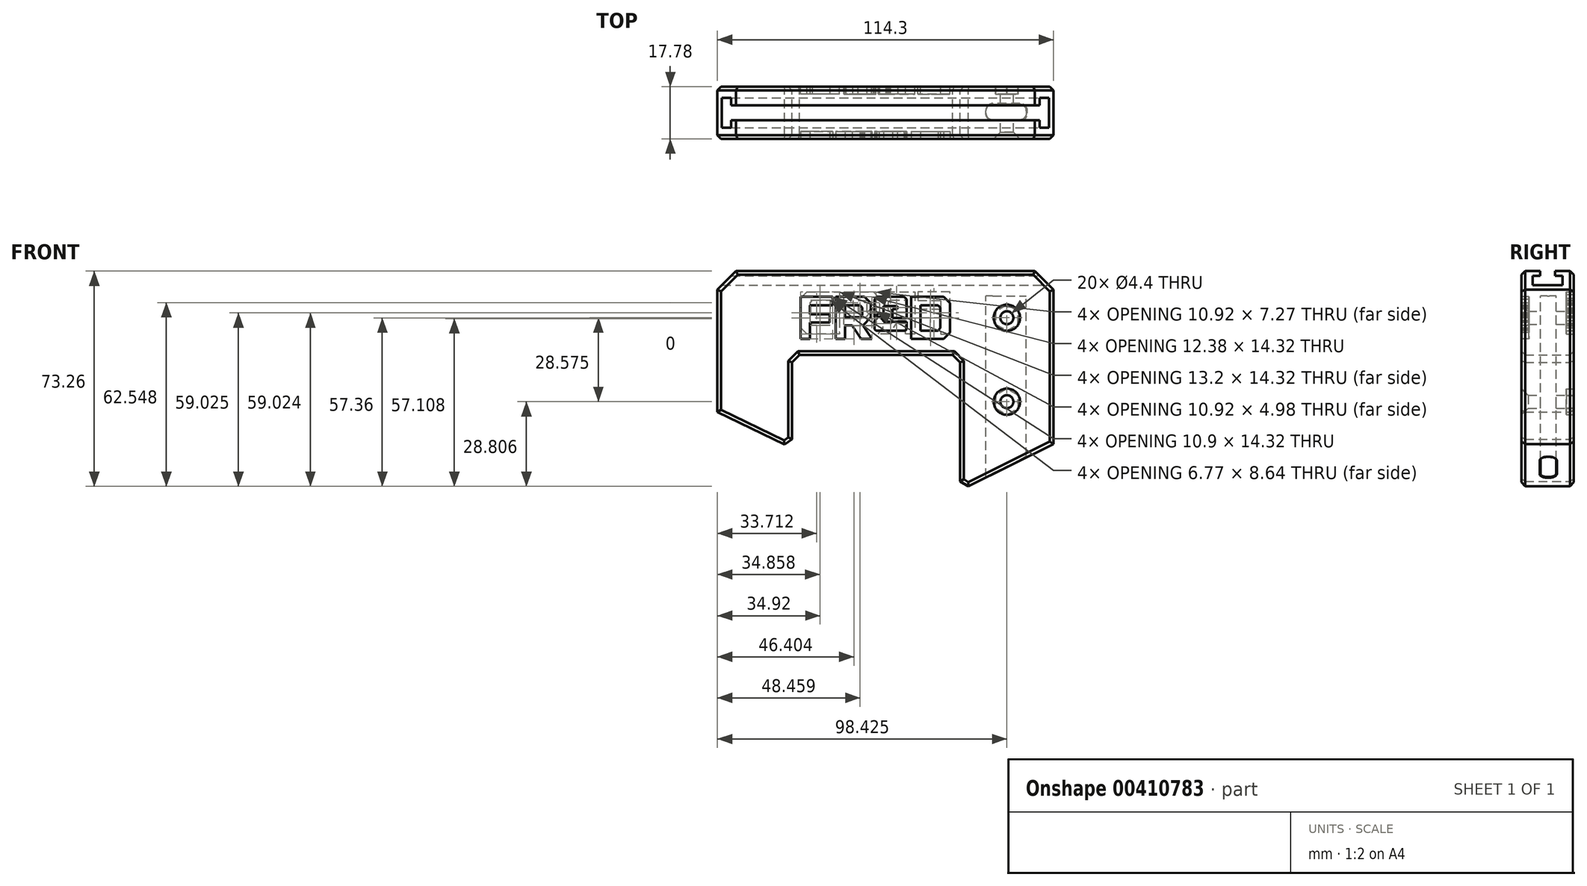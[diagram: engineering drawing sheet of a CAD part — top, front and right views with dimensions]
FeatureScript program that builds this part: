
annotation { "Feature Type Name" : "Feature", "Feature Type Description" : "" }
export const myFeature = defineFeature(function(context is Context, id is Id, definition is map)
    precondition{}
    {
        {
            var Q0;
            Q0=qCreatedBy(makeId("Front.planeOp"),FACE);
            var sketch = newSketch(context, id + "F0", { "sketchPlane" : qUnion([Q0])});
            skLineSegment(sketch, "E0", {"start": v(-47.31, 34.12) * mm, "end": v(54.29, 34.12) * mm});
            skLineSegment(sketch, "E1", {"start": v(60.64, 27.77) * mm, "end": v(60.64, -24.7) * mm});
            skLineSegment(sketch, "E2", {"start": v(60.64, -24.7) * mm, "end": v(31.6, -39.14) * mm});
            skLineSegment(sketch, "E3", {"start": v(28.89, -37.47) * mm, "end": v(28.89, 3) * mm});
            skLineSegment(sketch, "E4", {"start": v(26.35, 5.54) * mm, "end": v(-25.72, 5.54) * mm});
            skLineSegment(sketch, "E5", {"start": v(-28.26, 3) * mm, "end": v(-28.26, -23.14) * mm});
            skLineSegment(sketch, "E6", {"start": v(-30.87, -24.94) * mm, "end": v(-53.66, -13.83) * mm});
            skLineSegment(sketch, "E7", {"start": v(-53.66, -13.83) * mm, "end": v(-53.66, 27.77) * mm});
            skLineSegment(sketch, "E8", {"start": v(-30.87, -24.94) * mm, "end": v(-28.26, -23.14) * mm});
            skLineSegment(sketch, "E9", {"start": v(28.89, -37.47) * mm, "end": v(31.6, -39.14) * mm});
            skLineSegment(sketch, "E10", {"start": v(-53.66, 27.77) * mm, "end": v(-47.31, 34.12) * mm});
            skPoint(sketch, "E11.orphan", {"position": v(-53.66, 34.12) * mm});
            skLineSegment(sketch, "E12", {"start": v(54.29, 34.12) * mm, "end": v(60.64, 27.77) * mm});
            skPoint(sketch, "E13.orphan", {"position": v(60.64, 34.12) * mm});
            skLineSegment(sketch, "E14", {"start": v(-28.26, 3) * mm, "end": v(-25.72, 5.54) * mm});
            skPoint(sketch, "E15.orphan", {"position": v(-28.26, 5.54) * mm});
            skLineSegment(sketch, "E16", {"start": v(26.35, 5.54) * mm, "end": v(28.89, 3) * mm});
            skPoint(sketch, "E17.orphan", {"position": v(28.89, 5.54) * mm});
            skSolve(sketch);
        }
        {
            var Q0;
            Q0=makeQuery(id+"F0.imprint","IMPRINT",FACE,{"disambiguationData":[TD([[makeQuery(id+"F0.imprint","IMPRINT",EDGE,{"derivedFrom":sQuery(id+"F0.wireOp",EDGE,"E0")}),-1.0]])]});
            var Q1;
            Q1=makeQuery(id+"F0.imprint","IMPRINT",FACE,{"disambiguationData":[TD([[makeQuery(id+"F0.imprint","IMPRINT",EDGE,{"derivedFrom":sQuery(id+"F0.wireOp",EDGE,"ZEpFWphL-ozMd-Qc4S-y12z-fugVZn2PExex")}),1.0]])]});
            var Q2;
            Q2=makeQuery(id+"F0.imprint","IMPRINT",FACE,{"disambiguationData":[TD([[makeQuery(id+"F0.imprint","IMPRINT",EDGE,{"derivedFrom":sQuery(id+"F0.wireOp",EDGE,"a8f3txKb-fRa5-LG7a-W4z5-OOKFphKNCb56")}),1.0]])]});
            extrude(context, id + "F1", {"entities" : qUnion([Q0, Q1, Q2]), "depth" : 17.78 * mm, "offsetDistance" : 25.4 * mm, "symmetric" : true});
        }
        {
            var Q0;
            Q0=qCreatedBy(makeId("Top.planeOp"),FACE);
            var sketch = newSketch(context, id + "F2", { "sketchPlane" : qUnion([Q0])});
            skLineSegment(sketch, "E18.bottom", {"start": v(39.94, -2.42) * mm, "end": v(49.08, -2.42) * mm});
            skLineSegment(sketch, "E18.top", {"start": v(39.94, 2.92) * mm, "end": v(49.08, 2.92) * mm});
            skLineSegment(sketch, "E18.left", {"start": v(37.65, -0.13) * mm, "end": v(37.65, 0.63) * mm});
            skLineSegment(sketch, "E18.right", {"start": v(51.37, -0.13) * mm, "end": v(51.37, 0.63) * mm});
            skPoint(sketch, "E19.visualSharp", {"position": v(37.65, -2.42) * mm});
            skArc(sketch, "E19.filletArc", {"start": v(37.65, -0.13) * mm, "mid": v(38.32, -1.75) * mm, "end": v(39.94, -2.42) * mm});
            skPoint(sketch, "E20.visualSharp", {"position": v(37.65, 2.92) * mm});
            skArc(sketch, "E20.filletArc", {"start": v(39.94, 2.92) * mm, "mid": v(38.32, 2.25) * mm, "end": v(37.65, 0.63) * mm});
            skPoint(sketch, "E21.visualSharp", {"position": v(51.37, 2.92) * mm});
            skArc(sketch, "E21.filletArc", {"start": v(51.37, 0.63) * mm, "mid": v(50.7, 2.25) * mm, "end": v(49.08, 2.92) * mm});
            skPoint(sketch, "E22.visualSharp", {"position": v(51.37, -2.42) * mm});
            skArc(sketch, "E22.filletArc", {"start": v(49.08, -2.42) * mm, "mid": v(50.7, -1.75) * mm, "end": v(51.37, -0.13) * mm});
            skSolve(sketch);
        }
        {
            var Q0;
            Q0=makeQuery(id+"F2.imprint","IMPRINT",FACE,{"disambiguationData":[TD([[makeQuery(id+"F2.imprint","IMPRINT",EDGE,{"derivedFrom":sQuery(id+"F2.wireOp",EDGE,"E18.bottom")}),1.0]])]});
            extrude(context, id + "F3", {"entities" : qUnion([Q0]), "operationType" : NewBodyOperationType.REMOVE, "oppositeDirection" : true, "depth" : 59.33 * mm, "offsetDistance" : 25.4 * mm, "hasSecondDirection" : true, "secondDirectionOppositeDirection" : false, "secondDirectionDepth" : 25.65 * mm});
        }
        {
            var Q0;
            Q0=makeQuery(id+"F1.opExtrude","CAP_EDGE",EDGE,{"disambiguationData":[OSD([sQuery(id+"F0.wireOp",EDGE,"E0")])],"isStart":false});
            var Q1;
            Q1=makeQuery(id+"F1.opExtrude","CAP_EDGE",EDGE,{"disambiguationData":[OSD([sQuery(id+"F0.wireOp",EDGE,"E12")])],"isStart":false});
            var Q2;
            Q2=makeQuery(id+"F1.opExtrude","CAP_EDGE",EDGE,{"disambiguationData":[OSD([sQuery(id+"F0.wireOp",EDGE,"E1")])],"isStart":false});
            var Q3;
            Q3=makeQuery(id+"F1.opExtrude","CAP_EDGE",EDGE,{"disambiguationData":[OSD([sQuery(id+"F0.wireOp",EDGE,"E4")])],"isStart":false});
            var Q4;
            Q4=makeQuery(id+"F1.opExtrude","CAP_EDGE",EDGE,{"disambiguationData":[OSD([sQuery(id+"F0.wireOp",EDGE,"E16")])],"isStart":false});
            var Q5;
            Q5=makeQuery(id+"F1.opExtrude","CAP_EDGE",EDGE,{"disambiguationData":[OSD([sQuery(id+"F0.wireOp",EDGE,"E3")])],"isStart":false});
            var Q6;
            Q6=makeQuery(id+"F1.opExtrude","CAP_EDGE",EDGE,{"disambiguationData":[OSD([sQuery(id+"F0.wireOp",EDGE,"E9")])],"isStart":false});
            var Q7;
            Q7=makeQuery(id+"F1.opExtrude","CAP_EDGE",EDGE,{"disambiguationData":[OSD([sQuery(id+"F0.wireOp",EDGE,"E2")])],"isStart":false});
            var Q8;
            Q8=makeQuery(id+"F1.opExtrude","CAP_EDGE",EDGE,{"disambiguationData":[OSD([sQuery(id+"F0.wireOp",EDGE,"E1")])],"isStart":true});
            var Q9;
            Q9=makeQuery(id+"F1.opExtrude","CAP_EDGE",EDGE,{"disambiguationData":[OSD([sQuery(id+"F0.wireOp",EDGE,"E2")])],"isStart":true});
            var Q10;
            Q10=makeQuery(id+"F1.opExtrude","CAP_EDGE",EDGE,{"disambiguationData":[OSD([sQuery(id+"F0.wireOp",EDGE,"E12")])],"isStart":true});
            var Q11;
            Q11=makeQuery(id+"F1.opExtrude","CAP_EDGE",EDGE,{"disambiguationData":[OSD([sQuery(id+"F0.wireOp",EDGE,"E0")])],"isStart":true});
            var Q12;
            Q12=makeQuery(id+"F1.opExtrude","CAP_EDGE",EDGE,{"disambiguationData":[OSD([sQuery(id+"F0.wireOp",EDGE,"E3")])],"isStart":true});
            var Q13;
            Q13=makeQuery(id+"F1.opExtrude","CAP_EDGE",EDGE,{"disambiguationData":[OSD([sQuery(id+"F0.wireOp",EDGE,"E9")])],"isStart":true});
            var Q14;
            Q14=makeQuery(id+"F1.opExtrude","CAP_EDGE",EDGE,{"disambiguationData":[OSD([sQuery(id+"F0.wireOp",EDGE,"E16")])],"isStart":true});
            var Q15;
            Q15=makeQuery(id+"F1.opExtrude","CAP_EDGE",EDGE,{"disambiguationData":[OSD([sQuery(id+"F0.wireOp",EDGE,"E4")])],"isStart":true});
            var Q16;
            Q16=makeQuery(id+"F1.opExtrude","CAP_EDGE",EDGE,{"disambiguationData":[OSD([sQuery(id+"F0.wireOp",EDGE,"E14")])],"isStart":true});
            var Q17;
            Q17=makeQuery(id+"F1.opExtrude","CAP_EDGE",EDGE,{"disambiguationData":[OSD([sQuery(id+"F0.wireOp",EDGE,"E5")])],"isStart":true});
            var Q18;
            Q18=makeQuery(id+"F1.opExtrude","CAP_EDGE",EDGE,{"disambiguationData":[OSD([sQuery(id+"F0.wireOp",EDGE,"E8")])],"isStart":true});
            var Q19;
            Q19=makeQuery(id+"F1.opExtrude","CAP_EDGE",EDGE,{"disambiguationData":[OSD([sQuery(id+"F0.wireOp",EDGE,"E6")])],"isStart":true});
            var Q20;
            Q20=makeQuery(id+"F1.opExtrude","CAP_EDGE",EDGE,{"disambiguationData":[OSD([sQuery(id+"F0.wireOp",EDGE,"E7")])],"isStart":true});
            var Q21;
            Q21=makeQuery(id+"F1.opExtrude","CAP_EDGE",EDGE,{"disambiguationData":[OSD([sQuery(id+"F0.wireOp",EDGE,"E10")])],"isStart":true});
            var Q22;
            Q22=makeQuery(id+"F1.opExtrude","CAP_EDGE",EDGE,{"disambiguationData":[OSD([sQuery(id+"F0.wireOp",EDGE,"E10")])],"isStart":false});
            var Q23;
            Q23=makeQuery(id+"F1.opExtrude","CAP_EDGE",EDGE,{"disambiguationData":[OSD([sQuery(id+"F0.wireOp",EDGE,"E7")])],"isStart":false});
            var Q24;
            Q24=makeQuery(id+"F1.opExtrude","CAP_EDGE",EDGE,{"disambiguationData":[OSD([sQuery(id+"F0.wireOp",EDGE,"E6")])],"isStart":false});
            var Q25;
            Q25=makeQuery(id+"F1.opExtrude","CAP_EDGE",EDGE,{"disambiguationData":[OSD([sQuery(id+"F0.wireOp",EDGE,"E8")])],"isStart":false});
            var Q26;
            Q26=makeQuery(id+"F1.opExtrude","CAP_EDGE",EDGE,{"disambiguationData":[OSD([sQuery(id+"F0.wireOp",EDGE,"E5")])],"isStart":false});
            var Q27;
            Q27=makeQuery(id+"F1.opExtrude","CAP_EDGE",EDGE,{"disambiguationData":[OSD([sQuery(id+"F0.wireOp",EDGE,"E14")])],"isStart":false});
            chamfer(context, id + "F4", {"entities" : qUnion([Q0, Q1, Q2, Q3, Q4, Q5, Q6, Q7, Q8, Q9, Q10, Q11, Q12, Q13, Q14, Q15, Q16, Q17, Q18, Q19, Q20, Q21, Q22, Q23, Q24, Q25, Q26, Q27]), "width" : 1.27 * mm, "tangentPropagation" : true});
        }
        {
            var Q0;
            Q0=makeQuery(id+"F3.boolean.opBoolean","INTERSECT",EDGE,{"derivedFrom":[makeQuery(id+"F1.opExtrude","SWEPT_FACE",FACE,{"disambiguationData":[OSD([sQuery(id+"F0.wireOp",EDGE,"E2")])]}),makeQuery(id+"F3.opExtrude","SWEPT_FACE",FACE,{"disambiguationData":[OSD([sQuery(id+"F2.wireOp",EDGE,"E18.bottom")])]})]});
            chamfer(context, id + "F5", {"entities" : qUnion([Q0]), "width" : 0.25 * mm, "tangentPropagation" : true});
        }
        {
            var Q0;
            Q0=makeQuery(id+"F1.opExtrude","CAP_FACE",FACE,{"disambiguationData":[OSD([sQuery(id+"F0.wireOp",EDGE,"E0"),sQuery(id+"F0.wireOp",EDGE,"E1"),sQuery(id+"F0.wireOp",EDGE,"E2"),sQuery(id+"F0.wireOp",EDGE,"E3"),sQuery(id+"F0.wireOp",EDGE,"E4"),sQuery(id+"F0.wireOp",EDGE,"E5"),sQuery(id+"F0.wireOp",EDGE,"E6"),sQuery(id+"F0.wireOp",EDGE,"E7"),sQuery(id+"F0.wireOp",EDGE,"E8"),sQuery(id+"F0.wireOp",EDGE,"E9"),sQuery(id+"F0.wireOp",EDGE,"E10"),sQuery(id+"F0.wireOp",EDGE,"E12"),sQuery(id+"F0.wireOp",EDGE,"E14"),sQuery(id+"F0.wireOp",EDGE,"E16")])],"isStart":false});
            var sketch = newSketch(context, id + "F6", { "sketchPlane" : qUnion([Q0])});
            skCircle(sketch, "E23", {"center": v(44.76, 18.24) * mm, "radius": 1.9 * mm});
            skCircle(sketch, "E24", {"center": v(44.76, -10.33) * mm, "radius": 1.9 * mm});
            skSolve(sketch);
        }
        {
            var Q0;
            Q0=sQuery(id+"F6.wireOp",VERTEX,"E23.center");
            var Q1;
            Q1=sQuery(id+"F6.wireOp",VERTEX,"E24.center");
            var Q2;
            Q2=makeQuery(id+"F1.opExtrude","SWEPT_BODY",BODY,{"disambiguationData":[OSD([sQuery(id+"F0.wireOp",EDGE,"E0"),sQuery(id+"F0.wireOp",EDGE,"E1"),sQuery(id+"F0.wireOp",EDGE,"E2"),sQuery(id+"F0.wireOp",EDGE,"E3"),sQuery(id+"F0.wireOp",EDGE,"E4"),sQuery(id+"F0.wireOp",EDGE,"E5"),sQuery(id+"F0.wireOp",EDGE,"E6"),sQuery(id+"F0.wireOp",EDGE,"E7"),sQuery(id+"F0.wireOp",EDGE,"E8"),sQuery(id+"F0.wireOp",EDGE,"E9"),sQuery(id+"F0.wireOp",EDGE,"E10"),sQuery(id+"F0.wireOp",EDGE,"E12"),sQuery(id+"F0.wireOp",EDGE,"E14"),sQuery(id+"F0.wireOp",EDGE,"E16")])]});
            hole(context, id + "F7", {"style" : HoleStyle.C_SINK, "endStyle" : HoleEndStyle.THROUGH, "standardTappedOrClearance" : lookupTablePath({ "standard" : "ISO", "fit" : "Normal", "size" : "M4", "type" : "Clearance" }), "standardBlindInLast" : lookupTablePath({ "fit" : "Standard", "standard" : "ISO", "size" : "M4", "type" : "Clearance" }), "holeDiameter" : 4.4 * mm, "cSinkDiameter" : 8.96 * mm, "cSinkAngle" : 90 * degree, "isTappedThrough" : true, "tappedDepth" : 12.7 * mm, "tapClearance" : 3, "locations" : qUnion([Q0, Q1]), "scope" : qUnion([Q2]), "startStyle" : HoleStartStyle.PART});
        }
        {
            var Q0;
            Q0=makeQuery(id+"F1.opExtrude","CAP_FACE",FACE,{"disambiguationData":[OSD([sQuery(id+"F0.wireOp",EDGE,"E0"),sQuery(id+"F0.wireOp",EDGE,"E1"),sQuery(id+"F0.wireOp",EDGE,"E2"),sQuery(id+"F0.wireOp",EDGE,"E3"),sQuery(id+"F0.wireOp",EDGE,"E4"),sQuery(id+"F0.wireOp",EDGE,"E5"),sQuery(id+"F0.wireOp",EDGE,"E6"),sQuery(id+"F0.wireOp",EDGE,"E7"),sQuery(id+"F0.wireOp",EDGE,"E8"),sQuery(id+"F0.wireOp",EDGE,"E9"),sQuery(id+"F0.wireOp",EDGE,"E10"),sQuery(id+"F0.wireOp",EDGE,"E12"),sQuery(id+"F0.wireOp",EDGE,"E14"),sQuery(id+"F0.wireOp",EDGE,"E16")])],"isStart":true});
            var sketch = newSketch(context, id + "F8", { "sketchPlane" : qUnion([Q0])});
            skCircle(sketch, "E25.cCircle", {"center": v(-44.76, 18.24) * mm, "radius": 3.8 * mm, "construction": true});
            skLineSegment(sketch, "E25.0", {"start": v(-48.57, 16.04) * mm, "end": v(-48.57, 20.44) * mm});
            skLineSegment(sketch, "E25.1", {"start": v(-48.57, 20.44) * mm, "end": v(-44.76, 22.64) * mm});
            skLineSegment(sketch, "E25.2", {"start": v(-44.76, 22.64) * mm, "end": v(-40.95, 20.44) * mm});
            skLineSegment(sketch, "E25.3", {"start": v(-40.95, 20.44) * mm, "end": v(-40.95, 16.04) * mm});
            skLineSegment(sketch, "E25.4", {"start": v(-40.95, 16.04) * mm, "end": v(-44.76, 13.84) * mm});
            skLineSegment(sketch, "E25.5", {"start": v(-44.76, 13.84) * mm, "end": v(-48.57, 16.04) * mm});
            skPoint(sketch, "E25.0.midPoint", {"position": v(-48.57, 18.24) * mm});
            skCircle(sketch, "E26.cCircle", {"center": v(-44.76, -10.33) * mm, "radius": 3.81 * mm, "construction": true});
            skLineSegment(sketch, "E26.0", {"start": v(-48.54, -8.07) * mm, "end": v(-44.69, -5.94) * mm});
            skLineSegment(sketch, "E26.1", {"start": v(-44.69, -5.94) * mm, "end": v(-40.92, -8.2) * mm});
            skLineSegment(sketch, "E26.2", {"start": v(-40.92, -8.2) * mm, "end": v(-41, -12.6) * mm});
            skLineSegment(sketch, "E26.3", {"start": v(-41, -12.6) * mm, "end": v(-44.84, -14.73) * mm});
            skLineSegment(sketch, "E26.4", {"start": v(-44.84, -14.73) * mm, "end": v(-48.61, -12.47) * mm});
            skLineSegment(sketch, "E26.5", {"start": v(-48.61, -12.47) * mm, "end": v(-48.54, -8.07) * mm});
            skPoint(sketch, "E26.0.midPoint", {"position": v(-46.61, -7) * mm});
            skSolve(sketch);
        }
        {
            var Q0;
            Q0=makeQuery(id+"F8.imprint","IMPRINT",FACE,{"disambiguationData":[TD([[makeQuery(id+"F8.imprint","IMPRINT",EDGE,{"derivedFrom":sQuery(id+"F8.wireOp",EDGE,"E25.0")}),-1.0]])]});
            var Q1;
            Q1=makeQuery(id+"F8.imprint","IMPRINT",FACE,{"disambiguationData":[TD([[makeQuery(id+"F8.imprint","IMPRINT",EDGE,{"derivedFrom":sQuery(id+"F8.wireOp",EDGE,"E26.0")}),-1.0]])]});
            extrude(context, id + "F9", {"entities" : qUnion([Q0, Q1]), "operationType" : NewBodyOperationType.REMOVE, "oppositeDirection" : true, "depth" : 2.54 * mm, "offsetDistance" : 25.4 * mm});
        }
        {
            var Q0;
            Q0=makeQuery(id+"F1.opExtrude","CAP_FACE",FACE,{"disambiguationData":[OSD([sQuery(id+"F0.wireOp",EDGE,"E0"),sQuery(id+"F0.wireOp",EDGE,"E1"),sQuery(id+"F0.wireOp",EDGE,"E2"),sQuery(id+"F0.wireOp",EDGE,"E3"),sQuery(id+"F0.wireOp",EDGE,"E4"),sQuery(id+"F0.wireOp",EDGE,"E5"),sQuery(id+"F0.wireOp",EDGE,"E6"),sQuery(id+"F0.wireOp",EDGE,"E7"),sQuery(id+"F0.wireOp",EDGE,"E8"),sQuery(id+"F0.wireOp",EDGE,"E9"),sQuery(id+"F0.wireOp",EDGE,"E10"),sQuery(id+"F0.wireOp",EDGE,"E12"),sQuery(id+"F0.wireOp",EDGE,"E14"),sQuery(id+"F0.wireOp",EDGE,"E16")])],"isStart":false});
            var sketch = newSketch(context, id + "F10", { "sketchPlane" : qUnion([Q0])});
            skLineSegment(sketch, "E27", {"start": v(-25.4, 25.38) * mm, "end": v(-14.5, 25.38) * mm});
            skLineSegment(sketch, "E28", {"start": v(-14.5, 25.38) * mm, "end": v(-14.5, 22.52) * mm});
            skLineSegment(sketch, "E29", {"start": v(-14.5, 22.52) * mm, "end": v(-22.25, 22.52) * mm});
            skLineSegment(sketch, "E30", {"start": v(-22.25, 22.52) * mm, "end": v(-22.25, 19.47) * mm});
            skLineSegment(sketch, "E31", {"start": v(-22.25, 19.47) * mm, "end": v(-15.42, 19.47) * mm});
            skLineSegment(sketch, "E32", {"start": v(-15.42, 19.47) * mm, "end": v(-15.42, 16.6) * mm});
            skLineSegment(sketch, "E33", {"start": v(-15.42, 16.6) * mm, "end": v(-22.25, 16.6) * mm});
            skLineSegment(sketch, "E34", {"start": v(-22.25, 16.6) * mm, "end": v(-22.25, 11.06) * mm});
            skLineSegment(sketch, "E35", {"start": v(-22.25, 11.06) * mm, "end": v(-25.4, 11.06) * mm});
            skLineSegment(sketch, "E36", {"start": v(-25.4, 11.06) * mm, "end": v(-25.4, 25.38) * mm});
            skLineSegment(sketch, "E37", {"start": v(2.84, 16.91) * mm, "end": v(2.84, 17.23) * mm});
            skLineSegment(sketch, "E38", {"start": v(2.84, 17.23) * mm, "end": v(1.3, 18.8) * mm});
            skLineSegment(sketch, "E39", {"start": v(1.3, 18.8) * mm, "end": v(-0.26, 17.23) * mm});
            skLineSegment(sketch, "E40", {"start": v(-0.26, 17.23) * mm, "end": v(-0.26, 16.91) * mm});
            skLineSegment(sketch, "E41", {"start": v(-0.26, 16.91) * mm, "end": v(-0.26, 14.47) * mm});
            skLineSegment(sketch, "E42", {"start": v(-0.26, 14.47) * mm, "end": v(-0.26, 14.3) * mm});
            skLineSegment(sketch, "E43", {"start": v(-0.26, 14.3) * mm, "end": v(0.23, 13.81) * mm});
            skLineSegment(sketch, "E44", {"start": v(0.23, 13.81) * mm, "end": v(10.17, 13.81) * mm});
            skLineSegment(sketch, "E45", {"start": v(10.17, 13.81) * mm, "end": v(10.66, 14.3) * mm});
            skLineSegment(sketch, "E46", {"start": v(10.66, 14.3) * mm, "end": v(10.66, 16.91) * mm});
            skLineSegment(sketch, "E47", {"start": v(10.66, 16.91) * mm, "end": v(2.84, 16.91) * mm});
            skLineSegment(sketch, "E48", {"start": v(-0.26, 24.56) * mm, "end": v(-0.26, 22.28) * mm});
            skLineSegment(sketch, "E49", {"start": v(-0.26, 22.28) * mm, "end": v(-0.26, 18.38) * mm});
            skLineSegment(sketch, "E50", {"start": v(-0.26, 18.38) * mm, "end": v(1.3, 19.94) * mm});
            skLineSegment(sketch, "E51", {"start": v(1.3, 19.94) * mm, "end": v(2.84, 18.38) * mm});
            skLineSegment(sketch, "E52", {"start": v(2.84, 18.38) * mm, "end": v(2.84, 22.28) * mm});
            skLineSegment(sketch, "E53", {"start": v(2.84, 22.28) * mm, "end": v(7.56, 22.28) * mm});
            skLineSegment(sketch, "E54", {"start": v(7.56, 22.28) * mm, "end": v(7.56, 21.2) * mm});
            skLineSegment(sketch, "E55", {"start": v(7.56, 21.2) * mm, "end": v(5.87, 21.2) * mm});
            skLineSegment(sketch, "E56", {"start": v(5.87, 21.2) * mm, "end": v(5.87, 18.1) * mm});
            skLineSegment(sketch, "E57", {"start": v(5.87, 18.1) * mm, "end": v(10.66, 18.1) * mm});
            skLineSegment(sketch, "E58", {"start": v(10.66, 18.1) * mm, "end": v(10.66, 19.48) * mm});
            skLineSegment(sketch, "E59", {"start": v(10.66, 19.48) * mm, "end": v(10.66, 21.2) * mm});
            skLineSegment(sketch, "E60", {"start": v(10.66, 21.2) * mm, "end": v(10.66, 22.28) * mm});
            skLineSegment(sketch, "E61", {"start": v(10.66, 22.28) * mm, "end": v(10.66, 24.56) * mm});
            skLineSegment(sketch, "E62", {"start": v(10.66, 24.56) * mm, "end": v(9.84, 25.38) * mm});
            skLineSegment(sketch, "E63", {"start": v(9.84, 25.38) * mm, "end": v(2.84, 25.38) * mm});
            skLineSegment(sketch, "E64", {"start": v(2.84, 25.38) * mm, "end": v(0.56, 25.38) * mm});
            skLineSegment(sketch, "E65", {"start": v(0.56, 25.38) * mm, "end": v(-0.26, 24.56) * mm});
            skLineSegment(sketch, "E66", {"start": v(-4.22, 15.66) * mm, "end": v(-1.51, 18.46) * mm});
            skLineSegment(sketch, "E67", {"start": v(-1.51, 18.46) * mm, "end": v(-1.51, 23.23) * mm});
            skLineSegment(sketch, "E68", {"start": v(-1.51, 23.23) * mm, "end": v(-3.66, 25.38) * mm});
            skLineSegment(sketch, "E69", {"start": v(-3.66, 25.38) * mm, "end": v(-13.45, 25.38) * mm});
            skLineSegment(sketch, "E70", {"start": v(-13.45, 25.38) * mm, "end": v(-13.45, 11.06) * mm});
            skLineSegment(sketch, "E71", {"start": v(-13.45, 11.06) * mm, "end": v(-10.3, 11.06) * mm});
            skLineSegment(sketch, "E72", {"start": v(-10.3, 11.06) * mm, "end": v(-10.3, 15.64) * mm});
            skLineSegment(sketch, "E73", {"start": v(-10.3, 15.64) * mm, "end": v(-7.82, 15.64) * mm});
            skLineSegment(sketch, "E74", {"start": v(-7.82, 15.64) * mm, "end": v(-4.75, 11.06) * mm});
            skLineSegment(sketch, "E75", {"start": v(-4.75, 11.06) * mm, "end": v(-1.07, 11.06) * mm});
            skLineSegment(sketch, "E76", {"start": v(-1.07, 11.06) * mm, "end": v(-4.22, 15.66) * mm});
            skLineSegment(sketch, "E77", {"start": v(17.94, 11.06) * mm, "end": v(23.17, 11.06) * mm});
            skLineSegment(sketch, "E78", {"start": v(23.17, 11.06) * mm, "end": v(23.25, 11.06) * mm});
            skLineSegment(sketch, "E79", {"start": v(23.25, 11.06) * mm, "end": v(25.4, 13.2) * mm});
            skLineSegment(sketch, "E80", {"start": v(25.4, 13.2) * mm, "end": v(25.4, 17.98) * mm});
            skLineSegment(sketch, "E81", {"start": v(25.4, 17.98) * mm, "end": v(25.4, 18.46) * mm});
            skLineSegment(sketch, "E82", {"start": v(25.4, 18.46) * mm, "end": v(25.4, 23.23) * mm});
            skLineSegment(sketch, "E83", {"start": v(25.4, 23.23) * mm, "end": v(23.25, 25.38) * mm});
            skLineSegment(sketch, "E84", {"start": v(23.25, 25.38) * mm, "end": v(23.17, 25.38) * mm});
            skLineSegment(sketch, "E85", {"start": v(23.17, 25.38) * mm, "end": v(17.94, 25.38) * mm});
            skLineSegment(sketch, "E86", {"start": v(17.94, 25.38) * mm, "end": v(17.79, 25.38) * mm});
            skLineSegment(sketch, "E87", {"start": v(17.79, 25.38) * mm, "end": v(12.2, 25.38) * mm});
            skLineSegment(sketch, "E88", {"start": v(12.2, 25.38) * mm, "end": v(12.2, 11.06) * mm});
            skLineSegment(sketch, "E89", {"start": v(12.2, 11.06) * mm, "end": v(17.79, 11.06) * mm});
            skLineSegment(sketch, "E90", {"start": v(17.79, 11.06) * mm, "end": v(17.94, 11.06) * mm});
            skLineSegment(sketch, "E91", {"start": v(-5.22, 18.4) * mm, "end": v(-4.4, 19.2) * mm});
            skLineSegment(sketch, "E92", {"start": v(-4.4, 19.2) * mm, "end": v(-4.4, 21.72) * mm});
            skLineSegment(sketch, "E93", {"start": v(-4.4, 21.72) * mm, "end": v(-5.22, 22.54) * mm});
            skLineSegment(sketch, "E94", {"start": v(-5.22, 22.54) * mm, "end": v(-10.3, 22.54) * mm});
            skLineSegment(sketch, "E95", {"start": v(-10.3, 22.54) * mm, "end": v(-10.3, 18.4) * mm});
            skLineSegment(sketch, "E96", {"start": v(-10.3, 18.4) * mm, "end": v(-5.22, 18.4) * mm});
            skLineSegment(sketch, "E97", {"start": v(21.3, 13.9) * mm, "end": v(22.13, 14.72) * mm});
            skLineSegment(sketch, "E98", {"start": v(22.13, 14.72) * mm, "end": v(22.13, 21.72) * mm});
            skLineSegment(sketch, "E99", {"start": v(22.13, 21.72) * mm, "end": v(21.3, 22.54) * mm});
            skLineSegment(sketch, "E100", {"start": v(21.3, 22.54) * mm, "end": v(15.35, 22.54) * mm});
            skLineSegment(sketch, "E101", {"start": v(15.35, 22.54) * mm, "end": v(15.35, 13.9) * mm});
            skLineSegment(sketch, "E102", {"start": v(15.35, 13.9) * mm, "end": v(21.3, 13.9) * mm});
            skSolve(sketch);
        }
        {
            var Q0;
            Q0=makeQuery(id+"F10.imprint","IMPRINT",FACE,{"disambiguationData":[TD([[makeQuery(id+"F10.imprint","IMPRINT",EDGE,{"derivedFrom":sQuery(id+"F10.wireOp",EDGE,"E27")}),-1.0]])]});
            var Q1;
            Q1=makeQuery(id+"F10.imprint","IMPRINT",FACE,{"disambiguationData":[TD([[makeQuery(id+"F10.imprint","IMPRINT",EDGE,{"derivedFrom":sQuery(id+"F10.wireOp",EDGE,"E66")}),1.0]])]});
            var Q2;
            Q2=makeQuery(id+"F10.imprint","IMPRINT",FACE,{"disambiguationData":[TD([[makeQuery(id+"F10.imprint","IMPRINT",EDGE,{"derivedFrom":sQuery(id+"F10.wireOp",EDGE,"E48")}),1.0]])]});
            var Q3;
            Q3=makeQuery(id+"F10.imprint","IMPRINT",FACE,{"disambiguationData":[TD([[makeQuery(id+"F10.imprint","IMPRINT",EDGE,{"derivedFrom":sQuery(id+"F10.wireOp",EDGE,"E37")}),1.0]])]});
            var Q4;
            Q4=makeQuery(id+"F10.imprint","IMPRINT",FACE,{"disambiguationData":[TD([[makeQuery(id+"F10.imprint","IMPRINT",EDGE,{"derivedFrom":sQuery(id+"F10.wireOp",EDGE,"E77")}),1.0]])]});
            extrude(context, id + "F11", {"entities" : qUnion([Q0, Q1, Q2, Q3, Q4]), "operationType" : NewBodyOperationType.REMOVE, "oppositeDirection" : true, "depth" : 2.54 * mm, "offsetDistance" : 25.4 * mm});
        }
        {
            var Q0;
            Q0=makeQuery(id+"F1.opExtrude","CAP_FACE",FACE,{"disambiguationData":[OSD([sQuery(id+"F0.wireOp",EDGE,"E0"),sQuery(id+"F0.wireOp",EDGE,"E1"),sQuery(id+"F0.wireOp",EDGE,"E2"),sQuery(id+"F0.wireOp",EDGE,"E3"),sQuery(id+"F0.wireOp",EDGE,"E4"),sQuery(id+"F0.wireOp",EDGE,"E5"),sQuery(id+"F0.wireOp",EDGE,"E6"),sQuery(id+"F0.wireOp",EDGE,"E7"),sQuery(id+"F0.wireOp",EDGE,"E8"),sQuery(id+"F0.wireOp",EDGE,"E9"),sQuery(id+"F0.wireOp",EDGE,"E10"),sQuery(id+"F0.wireOp",EDGE,"E12"),sQuery(id+"F0.wireOp",EDGE,"E14"),sQuery(id+"F0.wireOp",EDGE,"E16")])],"isStart":true});
            var sketch = newSketch(context, id + "F12", { "sketchPlane" : qUnion([Q0])});
            skLineSegment(sketch, "E103", {"start": v(-25.4, 27.04) * mm, "end": v(-14.5, 27.04) * mm});
            skLineSegment(sketch, "E104", {"start": v(-14.5, 27.04) * mm, "end": v(-14.5, 24.18) * mm});
            skLineSegment(sketch, "E105", {"start": v(-14.5, 24.18) * mm, "end": v(-22.25, 24.18) * mm});
            skLineSegment(sketch, "E106", {"start": v(-22.25, 24.18) * mm, "end": v(-22.25, 21.13) * mm});
            skLineSegment(sketch, "E107", {"start": v(-22.25, 21.13) * mm, "end": v(-15.42, 21.13) * mm});
            skLineSegment(sketch, "E108", {"start": v(-15.42, 21.13) * mm, "end": v(-15.42, 18.27) * mm});
            skLineSegment(sketch, "E109", {"start": v(-15.42, 18.27) * mm, "end": v(-22.25, 18.27) * mm});
            skLineSegment(sketch, "E110", {"start": v(-22.25, 18.27) * mm, "end": v(-22.25, 12.72) * mm});
            skLineSegment(sketch, "E111", {"start": v(-22.25, 12.72) * mm, "end": v(-25.4, 12.72) * mm});
            skLineSegment(sketch, "E112", {"start": v(-25.4, 12.72) * mm, "end": v(-25.4, 27.04) * mm});
            skLineSegment(sketch, "E113", {"start": v(2.84, 18.58) * mm, "end": v(2.84, 18.9) * mm});
            skLineSegment(sketch, "E114", {"start": v(2.84, 18.9) * mm, "end": v(1.3, 20.46) * mm});
            skLineSegment(sketch, "E115", {"start": v(1.3, 20.46) * mm, "end": v(-0.26, 18.9) * mm});
            skLineSegment(sketch, "E116", {"start": v(-0.26, 18.9) * mm, "end": v(-0.26, 18.58) * mm});
            skLineSegment(sketch, "E117", {"start": v(-0.26, 18.58) * mm, "end": v(-0.26, 16.13) * mm});
            skLineSegment(sketch, "E118", {"start": v(-0.26, 16.13) * mm, "end": v(-0.26, 15.96) * mm});
            skLineSegment(sketch, "E119", {"start": v(-0.26, 15.96) * mm, "end": v(0.23, 15.48) * mm});
            skLineSegment(sketch, "E120", {"start": v(0.23, 15.48) * mm, "end": v(10.17, 15.48) * mm});
            skLineSegment(sketch, "E121", {"start": v(10.17, 15.48) * mm, "end": v(10.66, 15.97) * mm});
            skLineSegment(sketch, "E122", {"start": v(10.66, 15.97) * mm, "end": v(10.66, 18.58) * mm});
            skLineSegment(sketch, "E123", {"start": v(10.66, 18.58) * mm, "end": v(2.84, 18.58) * mm});
            skLineSegment(sketch, "E124", {"start": v(-0.26, 26.23) * mm, "end": v(-0.26, 23.94) * mm});
            skLineSegment(sketch, "E125", {"start": v(-0.26, 23.94) * mm, "end": v(-0.26, 20.04) * mm});
            skLineSegment(sketch, "E126", {"start": v(-0.26, 20.04) * mm, "end": v(1.3, 21.6) * mm});
            skLineSegment(sketch, "E127", {"start": v(1.3, 21.6) * mm, "end": v(2.84, 20.04) * mm});
            skLineSegment(sketch, "E128", {"start": v(2.84, 20.04) * mm, "end": v(2.84, 23.94) * mm});
            skLineSegment(sketch, "E129", {"start": v(2.84, 23.94) * mm, "end": v(7.56, 23.94) * mm});
            skLineSegment(sketch, "E130", {"start": v(7.56, 23.94) * mm, "end": v(7.56, 22.87) * mm});
            skLineSegment(sketch, "E131", {"start": v(7.56, 22.87) * mm, "end": v(5.87, 22.87) * mm});
            skLineSegment(sketch, "E132", {"start": v(5.87, 22.87) * mm, "end": v(5.87, 19.77) * mm});
            skLineSegment(sketch, "E133", {"start": v(5.87, 19.77) * mm, "end": v(10.66, 19.77) * mm});
            skLineSegment(sketch, "E134", {"start": v(10.66, 19.77) * mm, "end": v(10.66, 21.15) * mm});
            skLineSegment(sketch, "E135", {"start": v(10.66, 21.15) * mm, "end": v(10.66, 22.87) * mm});
            skLineSegment(sketch, "E136", {"start": v(10.66, 22.87) * mm, "end": v(10.66, 23.94) * mm});
            skLineSegment(sketch, "E137", {"start": v(10.66, 23.94) * mm, "end": v(10.66, 26.22) * mm});
            skLineSegment(sketch, "E138", {"start": v(10.66, 26.22) * mm, "end": v(9.84, 27.04) * mm});
            skLineSegment(sketch, "E139", {"start": v(9.84, 27.04) * mm, "end": v(2.84, 27.04) * mm});
            skLineSegment(sketch, "E140", {"start": v(2.84, 27.04) * mm, "end": v(0.56, 27.04) * mm});
            skLineSegment(sketch, "E141", {"start": v(0.56, 27.04) * mm, "end": v(-0.26, 26.23) * mm});
            skLineSegment(sketch, "E142", {"start": v(-4.22, 17.33) * mm, "end": v(-1.51, 20.13) * mm});
            skLineSegment(sketch, "E143", {"start": v(-1.51, 20.13) * mm, "end": v(-1.51, 24.9) * mm});
            skLineSegment(sketch, "E144", {"start": v(-1.51, 24.9) * mm, "end": v(-3.66, 27.04) * mm});
            skLineSegment(sketch, "E145", {"start": v(-3.66, 27.04) * mm, "end": v(-13.45, 27.04) * mm});
            skLineSegment(sketch, "E146", {"start": v(-13.45, 27.04) * mm, "end": v(-13.45, 12.72) * mm});
            skLineSegment(sketch, "E147", {"start": v(-13.45, 12.72) * mm, "end": v(-10.3, 12.72) * mm});
            skLineSegment(sketch, "E148", {"start": v(-10.3, 12.72) * mm, "end": v(-10.3, 17.3) * mm});
            skLineSegment(sketch, "E149", {"start": v(-10.3, 17.3) * mm, "end": v(-7.82, 17.3) * mm});
            skLineSegment(sketch, "E150", {"start": v(-7.82, 17.3) * mm, "end": v(-4.75, 12.72) * mm});
            skLineSegment(sketch, "E151", {"start": v(-4.75, 12.72) * mm, "end": v(-1.07, 12.72) * mm});
            skLineSegment(sketch, "E152", {"start": v(-1.07, 12.72) * mm, "end": v(-4.22, 17.33) * mm});
            skLineSegment(sketch, "E153", {"start": v(17.94, 12.72) * mm, "end": v(23.17, 12.72) * mm});
            skLineSegment(sketch, "E154", {"start": v(23.17, 12.72) * mm, "end": v(23.25, 12.72) * mm});
            skLineSegment(sketch, "E155", {"start": v(23.25, 12.72) * mm, "end": v(25.4, 14.87) * mm});
            skLineSegment(sketch, "E156", {"start": v(25.4, 14.87) * mm, "end": v(25.4, 19.64) * mm});
            skLineSegment(sketch, "E157", {"start": v(25.4, 19.64) * mm, "end": v(25.4, 20.13) * mm});
            skLineSegment(sketch, "E158", {"start": v(25.4, 20.13) * mm, "end": v(25.4, 24.9) * mm});
            skLineSegment(sketch, "E159", {"start": v(25.4, 24.9) * mm, "end": v(23.25, 27.04) * mm});
            skLineSegment(sketch, "E160", {"start": v(23.25, 27.04) * mm, "end": v(23.17, 27.04) * mm});
            skLineSegment(sketch, "E161", {"start": v(23.17, 27.04) * mm, "end": v(17.94, 27.04) * mm});
            skLineSegment(sketch, "E162", {"start": v(17.94, 27.04) * mm, "end": v(17.79, 27.04) * mm});
            skLineSegment(sketch, "E163", {"start": v(17.79, 27.04) * mm, "end": v(12.2, 27.04) * mm});
            skLineSegment(sketch, "E164", {"start": v(12.2, 27.04) * mm, "end": v(12.2, 12.72) * mm});
            skLineSegment(sketch, "E165", {"start": v(12.2, 12.72) * mm, "end": v(17.79, 12.72) * mm});
            skLineSegment(sketch, "E166", {"start": v(17.79, 12.72) * mm, "end": v(17.94, 12.72) * mm});
            skLineSegment(sketch, "E167", {"start": v(-5.22, 20.07) * mm, "end": v(-4.4, 20.87) * mm});
            skLineSegment(sketch, "E168", {"start": v(-4.4, 20.87) * mm, "end": v(-4.4, 23.39) * mm});
            skLineSegment(sketch, "E169", {"start": v(-4.4, 23.39) * mm, "end": v(-5.22, 24.2) * mm});
            skLineSegment(sketch, "E170", {"start": v(-5.22, 24.2) * mm, "end": v(-10.3, 24.2) * mm});
            skLineSegment(sketch, "E171", {"start": v(-10.3, 24.2) * mm, "end": v(-10.3, 20.07) * mm});
            skLineSegment(sketch, "E172", {"start": v(-10.3, 20.07) * mm, "end": v(-5.22, 20.07) * mm});
            skLineSegment(sketch, "E173", {"start": v(21.3, 15.57) * mm, "end": v(22.13, 16.39) * mm});
            skLineSegment(sketch, "E174", {"start": v(22.13, 16.39) * mm, "end": v(22.13, 23.39) * mm});
            skLineSegment(sketch, "E175", {"start": v(22.13, 23.39) * mm, "end": v(21.3, 24.2) * mm});
            skLineSegment(sketch, "E176", {"start": v(21.3, 24.2) * mm, "end": v(15.35, 24.2) * mm});
            skLineSegment(sketch, "E177", {"start": v(15.35, 24.2) * mm, "end": v(15.35, 15.57) * mm});
            skLineSegment(sketch, "E178", {"start": v(15.35, 15.57) * mm, "end": v(21.3, 15.57) * mm});
            skSolve(sketch);
        }
        {
            var Q0;
            Q0=makeQuery(id+"F12.imprint","IMPRINT",FACE,{"disambiguationData":[TD([[makeQuery(id+"F12.imprint","IMPRINT",EDGE,{"derivedFrom":sQuery(id+"F12.wireOp",EDGE,"E113")}),1.0]])]});
            var Q1;
            Q1=makeQuery(id+"F12.imprint","IMPRINT",FACE,{"disambiguationData":[TD([[makeQuery(id+"F12.imprint","IMPRINT",EDGE,{"derivedFrom":sQuery(id+"F12.wireOp",EDGE,"E124")}),1.0]])]});
            var Q2;
            Q2=makeQuery(id+"F12.imprint","IMPRINT",FACE,{"disambiguationData":[TD([[makeQuery(id+"F12.imprint","IMPRINT",EDGE,{"derivedFrom":sQuery(id+"F12.wireOp",EDGE,"E142")}),1.0]])]});
            var Q3;
            Q3=makeQuery(id+"F12.imprint","IMPRINT",FACE,{"disambiguationData":[TD([[makeQuery(id+"F12.imprint","IMPRINT",EDGE,{"derivedFrom":sQuery(id+"F12.wireOp",EDGE,"E153")}),1.0]])]});
            var Q4;
            Q4=makeQuery(id+"F12.imprint","IMPRINT",FACE,{"disambiguationData":[TD([[makeQuery(id+"F12.imprint","IMPRINT",EDGE,{"derivedFrom":sQuery(id+"F12.wireOp",EDGE,"E103")}),-1.0]])]});
            extrude(context, id + "F13", {"entities" : qUnion([Q0, Q1, Q2, Q3, Q4]), "operationType" : NewBodyOperationType.REMOVE, "oppositeDirection" : true, "depth" : 2.54 * mm, "offsetDistance" : 25.4 * mm});
        }
        {
            var Q0;
            Q0=qCreatedBy(makeId("Right.planeOp"),FACE);
            var sketch = newSketch(context, id + "F14", { "sketchPlane" : qUnion([Q0])});
            skLineSegment(sketch, "E179.bottom", {"start": v(-5.08, 32.47) * mm, "end": v(5.08, 32.47) * mm});
            skLineSegment(sketch, "E179.top", {"start": v(-5.08, 29.3) * mm, "end": v(5.08, 29.3) * mm});
            skLineSegment(sketch, "E179.left", {"start": v(-5.08, 32.47) * mm, "end": v(-5.08, 29.3) * mm});
            skLineSegment(sketch, "E179.right", {"start": v(5.08, 32.47) * mm, "end": v(5.08, 29.3) * mm});
            skPoint(sketch, "E179.middle", {"position": v(0, 34.12) * mm});
            skLineSegment(sketch, "E180.bottom", {"start": v(-2.54, 34.53) * mm, "end": v(2.54, 34.53) * mm});
            skLineSegment(sketch, "E180.top", {"start": v(-2.54, 30.4) * mm, "end": v(2.54, 30.4) * mm});
            skLineSegment(sketch, "E180.left", {"start": v(-2.54, 34.53) * mm, "end": v(-2.54, 30.4) * mm});
            skLineSegment(sketch, "E180.right", {"start": v(2.54, 34.53) * mm, "end": v(2.54, 30.4) * mm});
            skPoint(sketch, "E180.middle", {"position": v(0, 32.47) * mm});
            skSolve(sketch);
        }
        {
            var Q0;
            Q0=makeQuery(id+"F14.imprint","IMPRINT",FACE,{"disambiguationData":[TD([[makeQuery(id+"F14.imprint","IMPRINT",EDGE,{"derivedFrom":sQuery(id+"F14.wireOp",EDGE,"E179.top")}),1.0]])]});
            var Q1;
            {var subQ5=sQuery(id+"F14.wireOp",EDGE,"E180.bottom");Q1=makeQuery(id+"F14.imprint","IMPRINT",FACE,{"disambiguationData":[TD([[makeQuery(id+"F14.imprint","IMPRINT",EDGE,{"derivedFrom":subQ5}),-1.0]])]});}
            var Q2;
            {var subQ5=sQuery(id+"F14.wireOp",EDGE,"E180.top");Q2=makeQuery(id+"F14.imprint","IMPRINT",FACE,{"disambiguationData":[TD([[makeQuery(id+"F14.imprint","IMPRINT",EDGE,{"derivedFrom":subQ5}),1.0]])]});}
            extrude(context, id + "F15", {"entities" : qUnion([Q0, Q1, Q2]), "operationType" : NewBodyOperationType.REMOVE, "oppositeDirection" : true, "depth" : 142.75 * mm, "offsetDistance" : 25.4 * mm, "symmetric" : true});
        }
    });
